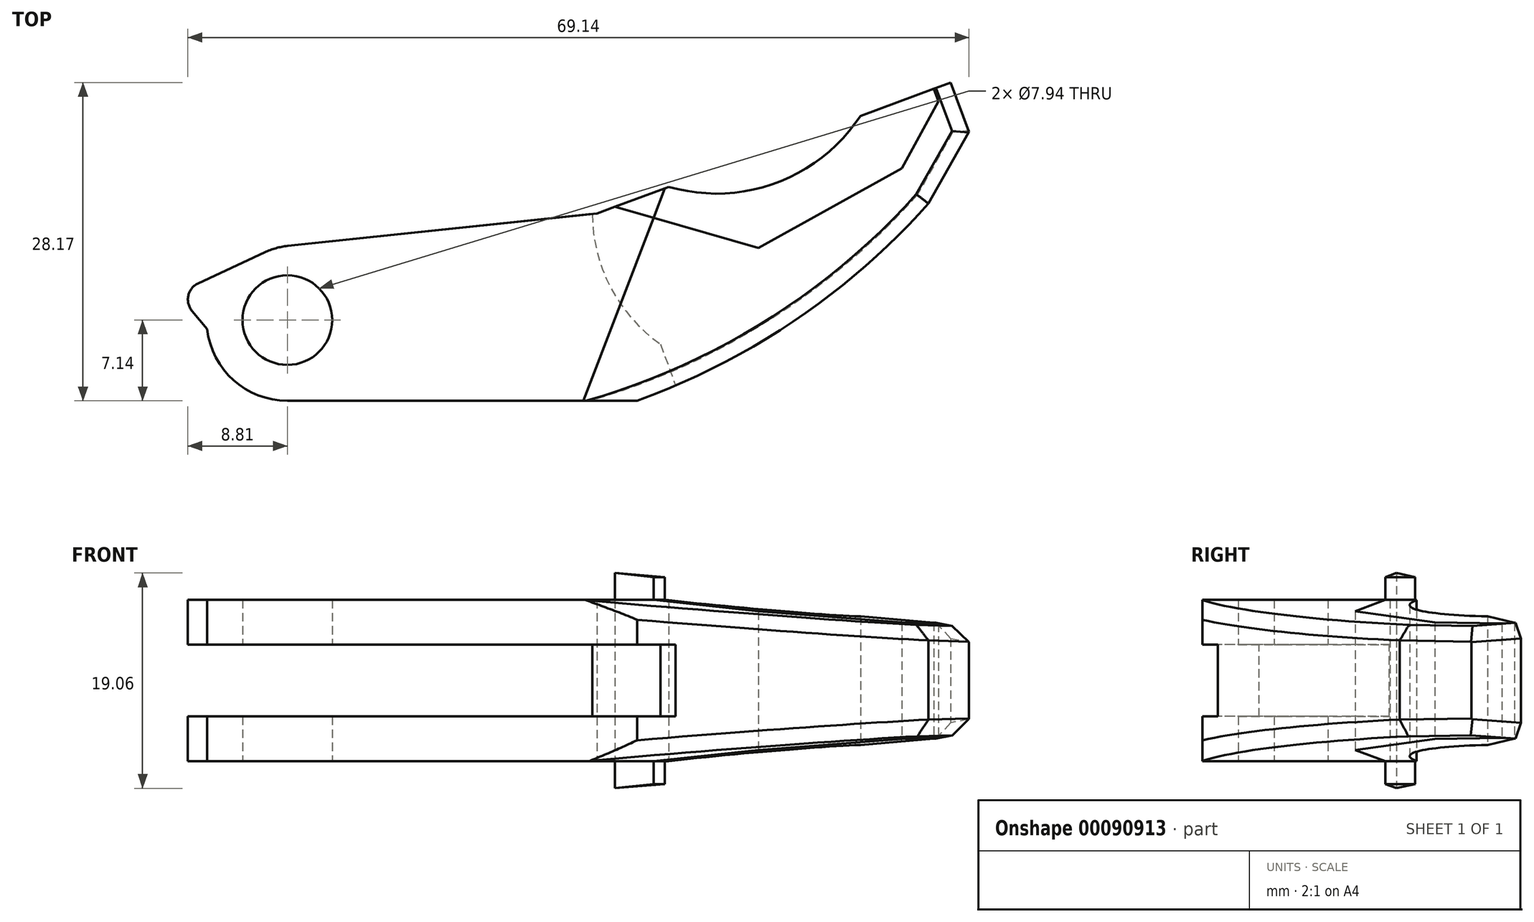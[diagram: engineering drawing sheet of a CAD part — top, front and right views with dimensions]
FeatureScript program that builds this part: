
annotation { "Feature Type Name" : "Feature", "Feature Type Description" : "" }
export const myFeature = defineFeature(function(context is Context, id is Id, definition is map)
    precondition{}
    {
        {
            var Q0;
            Q0=qCreatedBy(makeId("Top.planeOp"),FACE);
            var sketch = newSketch(context, id + "F0", { "sketchPlane" : qUnion([Q0])});
            skCircle(sketch, "E0", {"center": v(0, 0) * mm, "radius": 3.97 * mm});
            skLineSegment(sketch, "E1", {"start": v(0, 0) * mm, "end": v(55.48, 0) * mm, "construction": true});
            skLineSegment(sketch, "E2", {"start": v(0, -7.14) * mm, "end": v(26.2, -7.14) * mm});
            skArc(sketch, "E3", {"start": v(0, -7.14) * mm, "mid": v(-4.76, -5.32) * mm, "end": v(-7.1, -0.8) * mm});
            skLineSegment(sketch, "E4", {"start": v(-7.1, -0.8) * mm, "end": v(-8.43, 0.8) * mm});
            skLineSegment(sketch, "E5", {"start": v(-7.89, 3.26) * mm, "end": v(-2, 6) * mm});
            skLineSegment(sketch, "E6", {"start": v(0.02, 6.56) * mm, "end": v(27.4, 9.44) * mm});
            skPoint(sketch, "E7.visualSharp", {"position": v(-9.76, 2.38) * mm});
            skArc(sketch, "E7.filletArc", {"start": v(-7.89, 3.26) * mm, "mid": v(-8.77, 2.16) * mm, "end": v(-8.43, 0.8) * mm});
            skPoint(sketch, "E8.visualSharp", {"position": v(-1.03, 6.45) * mm});
            skArc(sketch, "E8.filletArc", {"start": v(0.02, 6.56) * mm, "mid": v(-1, 6.37) * mm, "end": v(-2, 6) * mm});
            skLineSegment(sketch, "E9", {"start": v(26.2, -7.14) * mm, "end": v(30.96, -7.14) * mm});
            skLineSegment(sketch, "E10", {"start": v(28.99, 10.03) * mm, "end": v(41.69, 6.39) * mm});
            skLineSegment(sketch, "E11", {"start": v(41.69, 6.39) * mm, "end": v(54.39, 13.43) * mm});
            skLineSegment(sketch, "E12", {"start": v(27.4, 9.44) * mm, "end": v(28.99, 10.03) * mm});
            skLineSegment(sketch, "E13", {"start": v(57.22, 20.48) * mm, "end": v(58.7, 21.03) * mm});
            skPoint(sketch, "E14.third.point", {"position": v(36.48, 41.56) * mm});
            skLineSegment(sketch, "E15", {"start": v(54.39, 13.43) * mm, "end": v(57.63, 19.37) * mm});
            skLineSegment(sketch, "E16", {"start": v(57.63, 19.37) * mm, "end": v(57.22, 20.48) * mm});
            skLineSegment(sketch, "E17", {"start": v(56.75, 10.32) * mm, "end": v(60.33, 16.67) * mm});
            skLineSegment(sketch, "E18", {"start": v(60.33, 16.67) * mm, "end": v(58.7, 21.03) * mm});
            skLineSegment(sketch, "E19", {"start": v(32.4, 9.05) * mm, "end": v(26.2, -7.14) * mm, "construction": true});
            skLineSegment(sketch, "E20", {"start": v(27.4, 9.44) * mm, "end": v(58.7, 21.03) * mm, "construction": true});
            skArc(sketch, "E21", {"start": v(30.96, -7.14) * mm, "mid": v(44.94, -0.02) * mm, "end": v(56.75, 10.32) * mm});
            skLineSegment(sketch, "E22", {"start": v(-14.92, 17.4) * mm, "end": v(62.6, -12.35) * mm, "construction": true});
            skSolve(sketch);
        }
        {
            var Q0;
            Q0=qCreatedBy(makeId("Top.planeOp"),FACE);
            var sketch = newSketch(context, id + "F1", { "sketchPlane" : qUnion([Q0])});
            skLineSegment(sketch, "E23", {"start": v(28.99, 10.03) * mm, "end": v(41.69, 6.39) * mm});
            skLineSegment(sketch, "E24", {"start": v(41.69, 6.39) * mm, "end": v(54.39, 13.43) * mm});
            skLineSegment(sketch, "E25", {"start": v(28.99, 10.03) * mm, "end": v(33.75, 11.8) * mm});
            skLineSegment(sketch, "E26", {"start": v(50.74, 18.08) * mm, "end": v(57.22, 20.48) * mm});
            skArc(sketch, "E27", {"start": v(33.75, 11.8) * mm, "mid": v(43.28, 12.14) * mm, "end": v(50.74, 18.08) * mm});
            skLineSegment(sketch, "E28", {"start": v(54.39, 13.43) * mm, "end": v(57.63, 19.37) * mm});
            skLineSegment(sketch, "E29", {"start": v(57.63, 19.37) * mm, "end": v(57.22, 20.48) * mm});
            skSolve(sketch);
        }
        {
            var Q0;
            Q0 = qSketchRegion(id + "F0", true);
            extrude(context, id + "F2", {"entities" : qUnion([Q0]), "endBound" : BoundingType.SYMMETRIC, "depth" : 14.29 * mm});
        }
        {
            var Q0;
            Q0 = qSketchRegion(id + "F1", true);
            extrude(context, id + "F3", {"entities" : qUnion([Q0]), "endBound" : BoundingType.SYMMETRIC, "depth" : 19.05 * mm});
        }
        {
            var Q0;
            Q0=sQuery(id+"F0.wireOp",EDGE,"E19");
            var Q1;
            Q1=sQuery(id+"F0.wireOp",VERTEX,"E9.start");
            var Q2;
            Q2 = qBodyType(qCreatedBy(id + "F5" ,EDGE), BodyType.WIRE);
            cPlane(context, id + "F4", {"entities" : qUnion([Q0, Q1, Q2]), "cplaneType" : CPlaneType.LINE_POINT, "offset" : 152.4 * mm, "width" : 152.4 * mm, "height" : 152.4 * mm});
        }
        {
            var Q0;
            Q0=qCreatedBy(id+"F4.planeOp",FACE);
            var sketch = newSketch(context, id + "F5", { "sketchPlane" : qUnion([Q0])});
            skLineSegment(sketch, "E30", {"start": v(23.47, 9.53) * mm, "end": v(64.9, 5.17) * mm});
            skLineSegment(sketch, "E31", {"start": v(27.01, 0) * mm, "end": v(27.01, 16.27) * mm, "construction": true});
            skLineSegment(sketch, "E32", {"start": v(27.01, 7.14) * mm, "end": v(65.82, 3.07) * mm});
            skLineSegment(sketch, "E33", {"start": v(27.01, 7.14) * mm, "end": v(27.01, 12.42) * mm});
            skLineSegment(sketch, "E34", {"start": v(27.01, 12.42) * mm, "end": v(65.82, 12.42) * mm});
            skLineSegment(sketch, "E35", {"start": v(65.82, 12.42) * mm, "end": v(65.82, 3.07) * mm});
            skLineSegment(sketch, "E36", {"start": v(23.47, 9.53) * mm, "end": v(23.47, 14.54) * mm});
            skLineSegment(sketch, "E37", {"start": v(23.47, 14.54) * mm, "end": v(64.9, 14.54) * mm});
            skLineSegment(sketch, "E38", {"start": v(64.9, 14.54) * mm, "end": v(64.9, 5.17) * mm});
            skLineSegment(sketch, "E39.MirrorCS", {"start": v(23.47, -14.54) * mm, "end": v(64.9, -14.54) * mm});
            skLineSegment(sketch, "E40.MirrorCS", {"start": v(27.01, -12.42) * mm, "end": v(65.82, -12.42) * mm});
            skLineSegment(sketch, "E41.MirrorCS", {"start": v(23.47, -9.53) * mm, "end": v(23.47, -14.54) * mm});
            skLineSegment(sketch, "E42.MirrorCS", {"start": v(27.01, -7.14) * mm, "end": v(27.01, -12.42) * mm});
            skLineSegment(sketch, "E43.MirrorCS", {"start": v(23.47, -9.53) * mm, "end": v(64.9, -5.17) * mm});
            skLineSegment(sketch, "E44.MirrorCS", {"start": v(27.01, -7.14) * mm, "end": v(65.82, -3.07) * mm});
            skLineSegment(sketch, "E45.MirrorCS", {"start": v(65.82, -12.42) * mm, "end": v(65.82, -3.07) * mm});
            skLineSegment(sketch, "E46.MirrorCS", {"start": v(64.9, -14.54) * mm, "end": v(64.9, -5.17) * mm});
            skSolve(sketch);
        }
        {
            var Q0;
            {var subQ0=sQuery(id+"F5.wireOp",EDGE,"E38");var subQ1=sQuery(id+"F5.wireOp",EDGE,"E30");var subQ2=makeQuery(id+"F5.imprint","INTERSECT",VERTEX,{"derivedFrom":[subQ1,subQ0]});Q0=makeQuery(id+"F5.imprint","IMPRINT",FACE,{"disambiguationData":[TD([[makeQuery(id+"F5.imprint","IMPRINT",EDGE,{"disambiguationData":[TD([[subQ2,1.0]])],"derivedFrom":subQ1}),1.0]])]});}
            var Q1;
            {var subQ0=sQuery(id+"F5.wireOp",EDGE,"E36");Q1=makeQuery(id+"F5.imprint","IMPRINT",FACE,{"disambiguationData":[TD([[makeQuery(id+"F5.imprint","IMPRINT",EDGE,{"derivedFrom":subQ0}),-1.0]])]});}
            extrude(context, id + "F6", {"entities" : qUnion([Q0, Q1]), "operationType" : NewBodyOperationType.REMOVE, "oppositeDirection" : true, "depth" : 41.65 * mm});
        }
        {
            var Q0;
            {var subQ5=sQuery(id+"F5.wireOp",EDGE,"E32");Q0=makeQuery(id+"F5.imprint","IMPRINT",FACE,{"disambiguationData":[TD([[makeQuery(id+"F5.imprint","IMPRINT",EDGE,{"derivedFrom":subQ5}),1.0]])]});}
            var Q1;
            {var subQ0=sQuery(id+"F5.wireOp",EDGE,"E38");var subQ1=sQuery(id+"F5.wireOp",EDGE,"E30");var subQ2=makeQuery(id+"F5.imprint","INTERSECT",VERTEX,{"derivedFrom":[subQ1,subQ0]});Q1=makeQuery(id+"F5.imprint","IMPRINT",FACE,{"disambiguationData":[TD([[makeQuery(id+"F5.imprint","IMPRINT",EDGE,{"disambiguationData":[TD([[subQ2,1.0]])],"derivedFrom":subQ1}),1.0]])]});}
            extrude(context, id + "F7", {"entities" : qUnion([Q0, Q1]), "operationType" : NewBodyOperationType.REMOVE, "oppositeDirection" : true, "depth" : 41.93 * mm});
        }
        {
            var Q0;
            {var subQ0=sQuery(id+"F5.wireOp",EDGE,"E42.MirrorCS");var subQ1=sQuery(id+"F5.wireOp",EDGE,"E40.MirrorCS");var subQ2=makeQuery(id+"F5.imprint","INTERSECT",VERTEX,{"derivedFrom":[subQ1,subQ0]});Q0=makeQuery(id+"F5.imprint","IMPRINT",FACE,{"disambiguationData":[TD([[makeQuery(id+"F5.imprint","IMPRINT",EDGE,{"disambiguationData":[TD([[subQ2,-1.0]])],"derivedFrom":subQ1}),1.0]])]});}
            var Q1;
            {var subQ8=sQuery(id+"F5.wireOp",EDGE,"E39.MirrorCS");Q1=makeQuery(id+"F5.imprint","IMPRINT",FACE,{"disambiguationData":[TD([[makeQuery(id+"F5.imprint","IMPRINT",EDGE,{"derivedFrom":subQ8}),1.0]])]});}
            extrude(context, id + "F8", {"entities" : qUnion([Q0, Q1]), "operationType" : NewBodyOperationType.REMOVE, "oppositeDirection" : true, "depth" : 44.1 * mm});
        }
        {
            var Q0;
            {var subQ0=sQuery(id+"F5.wireOp",EDGE,"E44.MirrorCS");Q0=makeQuery(id+"F5.imprint","IMPRINT",FACE,{"disambiguationData":[TD([[makeQuery(id+"F5.imprint","IMPRINT",EDGE,{"derivedFrom":subQ0}),-1.0]])]});}
            var Q1;
            {var subQ0=sQuery(id+"F5.wireOp",EDGE,"E42.MirrorCS");var subQ1=sQuery(id+"F5.wireOp",EDGE,"E40.MirrorCS");var subQ2=makeQuery(id+"F5.imprint","INTERSECT",VERTEX,{"derivedFrom":[subQ1,subQ0]});Q1=makeQuery(id+"F5.imprint","IMPRINT",FACE,{"disambiguationData":[TD([[makeQuery(id+"F5.imprint","IMPRINT",EDGE,{"disambiguationData":[TD([[subQ2,-1.0]])],"derivedFrom":subQ1}),1.0]])]});}
            extrude(context, id + "F9", {"entities" : qUnion([Q0, Q1]), "operationType" : NewBodyOperationType.REMOVE, "oppositeDirection" : true, "depth" : 41.6 * mm});
        }
        {
            var Q0;
            Q0=qCreatedBy(makeId("Top.planeOp"),FACE);
            var sketch = newSketch(context, id + "F10", { "sketchPlane" : qUnion([Q0])});
            skArc(sketch, "E47", {"start": v(27.14, 11.6) * mm, "mid": v(28.14, 3.9) * mm, "end": v(33.02, -2.14) * mm});
            skLineSegment(sketch, "E48", {"start": v(33.02, -2.14) * mm, "end": v(35.05, -7.62) * mm});
            skLineSegment(sketch, "E49", {"start": v(35.05, -7.62) * mm, "end": v(-10.56, -7.62) * mm});
            skLineSegment(sketch, "E50", {"start": v(-10.56, -7.62) * mm, "end": v(-10.56, 11.6) * mm});
            skLineSegment(sketch, "E51", {"start": v(-10.56, 11.6) * mm, "end": v(27.14, 11.6) * mm});
            skSolve(sketch);
        }
        {
            var Q0;
            Q0=makeQuery(id+"F10.imprint","IMPRINT",FACE,{"disambiguationData":[TD([[makeQuery(id+"F10.imprint","IMPRINT",EDGE,{"derivedFrom":sQuery(id+"F10.wireOp",EDGE,"E47")}),-1.0]])]});
            extrude(context, id + "F11", {"entities" : qUnion([Q0]), "operationType" : NewBodyOperationType.REMOVE, "endBound" : BoundingType.SYMMETRIC, "oppositeDirection" : true, "depth" : 6.35 * mm});
        }
        {
            var Q0;
            Q0=makeQuery(id+"F7.boolean.opBoolean","INTERSECT",EDGE,{"derivedFrom":[makeQuery(id+"F2.opExtrude","SWEPT_FACE",FACE,{"disambiguationData":[OSD([sQuery(id+"F0.wireOp",EDGE,"E18")])]}),makeQuery(id+"F7.opExtrude","SWEPT_FACE",FACE,{"disambiguationData":[OSD([sQuery(id+"F5.wireOp",EDGE,"E32")])]})]});
            var Q1;
            Q1=makeQuery(id+"F7.boolean.opBoolean","INTERSECT",EDGE,{"derivedFrom":[makeQuery(id+"F2.opExtrude","SWEPT_FACE",FACE,{"disambiguationData":[OSD([sQuery(id+"F0.wireOp",EDGE,"E17")])]}),makeQuery(id+"F7.opExtrude","SWEPT_FACE",FACE,{"disambiguationData":[OSD([sQuery(id+"F5.wireOp",EDGE,"E32")])]})]});
            var Q2;
            Q2=makeQuery(id+"F7.boolean.opBoolean","INTERSECT",EDGE,{"derivedFrom":[makeQuery(id+"F2.opExtrude","SWEPT_FACE",FACE,{"disambiguationData":[OSD([sQuery(id+"F0.wireOp",EDGE,"E21")])]}),makeQuery(id+"F7.opExtrude","SWEPT_FACE",FACE,{"disambiguationData":[OSD([sQuery(id+"F5.wireOp",EDGE,"E32")])]})]});
            var Q3;
            Q3=makeQuery(id+"F9.boolean.opBoolean","INTERSECT",EDGE,{"derivedFrom":[makeQuery(id+"F2.opExtrude","SWEPT_FACE",FACE,{"disambiguationData":[OSD([sQuery(id+"F0.wireOp",EDGE,"E18")])]}),makeQuery(id+"F9.opExtrude","SWEPT_FACE",FACE,{"disambiguationData":[OSD([sQuery(id+"F5.wireOp",EDGE,"E44.MirrorCS")])]})]});
            var Q4;
            Q4=makeQuery(id+"F9.boolean.opBoolean","INTERSECT",EDGE,{"derivedFrom":[makeQuery(id+"F2.opExtrude","SWEPT_FACE",FACE,{"disambiguationData":[OSD([sQuery(id+"F0.wireOp",EDGE,"E17")])]}),makeQuery(id+"F9.opExtrude","SWEPT_FACE",FACE,{"disambiguationData":[OSD([sQuery(id+"F5.wireOp",EDGE,"E44.MirrorCS")])]})]});
            var Q5;
            Q5=makeQuery(id+"F9.boolean.opBoolean","INTERSECT",EDGE,{"derivedFrom":[makeQuery(id+"F2.opExtrude","SWEPT_FACE",FACE,{"disambiguationData":[OSD([sQuery(id+"F0.wireOp",EDGE,"E21")])]}),makeQuery(id+"F9.opExtrude","SWEPT_FACE",FACE,{"disambiguationData":[OSD([sQuery(id+"F5.wireOp",EDGE,"E44.MirrorCS")])]})]});
            chamfer(context, id + "F12", {"entities" : qUnion([Q0, Q1, Q2, Q3, Q4, Q5]), "chamferType" : ChamferType.OFFSET_ANGLE, "width" : 1.27 * mm, "oppositeDirection" : false, "angle" : 45 * degree, "tangentPropagation" : true});
        }
    });
